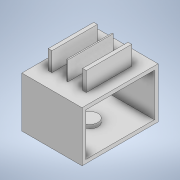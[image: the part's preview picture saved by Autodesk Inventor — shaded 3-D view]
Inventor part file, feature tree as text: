
AUTODESK INVENTOR PART (.ipt)
format: ipt  version: 2020 (Build 240168000, 168)  size: 191,488 bytes
history: native  units: mm
features: extrude x7, sketch x7
ambient origin geometry x8: Origin, YZ Plane, XZ Plane, XY Plane, X Axis, Y Axis, Z Axis, Center Point
bodies: Solid1 (feature_tree)
feature tree (14):
  extrude  "Extrusion1"  Depth=12.0mm
  extrude  "Extrusion2"  Depth=37.0mm
  extrude  "Extrusion3"  TaperAngle=0.0deg  [1 undecoded]
  extrude  "Extrusion4"  Depth=18.5mm
  extrude  "Extrusion7"  Depth=3.0mm
  extrude  "Extrusion8"  TaperAngle=0.0deg  [1 undecoded]
  extrude  "Extrusion9"  Depth=56.0mm
  sketch  "Sketch1"  dims[d0=12.0mm d1=12.0mm]
  sketch  "Sketch2"  dims[d2=1.0mm d3=37.0mm]
  sketch  "Sketch7"  dims[d8=3.0mm d9=3.0mm]
  sketch  "Sketch8"  dims[d10=0.0mm d11=0.0mm]
  sketch  "Sketch9"  dims[d12=15.5mm d13=0.0mm d14=56.0mm d15=28.0mm d16=9.0mm d17=9.0mm d18=3.0mm d19=3.0mm d20=3.0mm d21=0.0mm d22=56.0mm d23=28.0mm d26=3.0mm d27=3.0mm d28=35.0mm d29=0.0mm d30=56.0mm d31=28.0mm d34=3.0mm d35=3.0mm d36=3.0mm d37=0.0mm d45=13.0mm d46=6.0mm d47=0.0mm d48=7.5mm d49=10.0mm d50=5.0mm d51=0.0mm d52=13.0mm d53=10.0mm d54=7.5mm d55=5.0mm d56=0.0mm]
  sketch  "Sketch3"  dims[d4=37.0mm d5=0.0mm]
  sketch  "Sketch4"  dims[d6=0.5mm d7=18.5mm]
note: 2 required parameter values undecoded (feature->parameter linkage not recoverable at this tier; creation-order binding heuristic only, values carry confidence <= 0.55)
